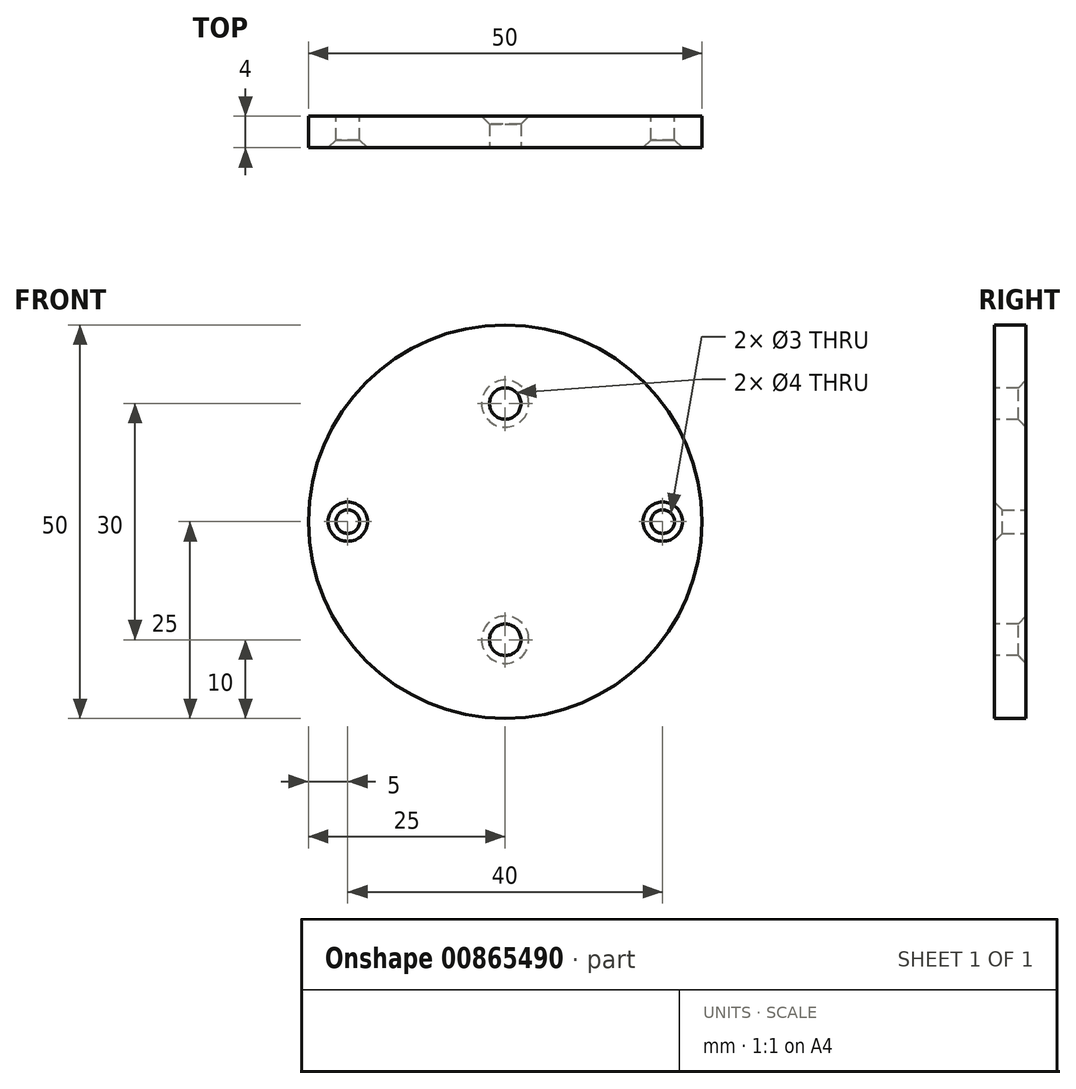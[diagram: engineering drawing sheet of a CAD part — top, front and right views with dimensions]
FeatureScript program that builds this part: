
annotation { "Feature Type Name" : "Feature", "Feature Type Description" : "" }
export const myFeature = defineFeature(function(context is Context, id is Id, definition is map)
    precondition{}
    {
        {
            var Q0;
            Q0=qCreatedBy(makeId("Front.planeOp"),FACE);
            var sketch = newSketch(context, id + "F0", { "sketchPlane" : qUnion([Q0])});
            skCircle(sketch, "E0", {"center": v(0, 0) * mm, "radius": 25 * mm});
            skCircle(sketch, "E1", {"center": v(20, 0) * mm, "radius": 1.5 * mm});
            skCircle(sketch, "E2", {"center": v(-20, 0) * mm, "radius": 1.5 * mm});
            skSolve(sketch);
        }
        {
            var Q0;
            Q0=makeQuery(id+"F0.imprint","IMPRINT",FACE,{"disambiguationData":[TD([[makeQuery(id+"F0.imprint","IMPRINT",EDGE,{"derivedFrom":sQuery(id+"F0.wireOp",EDGE,"E0")}),1.0]])]});
            extrude(context, id + "F1", {"entities" : qUnion([Q0]), "depth" : 4 * mm, "offsetDistance" : 25 * mm});
        }
        {
            var Q0;
            Q0=makeQuery(id+"F1.opExtrude","CAP_EDGE",EDGE,{"disambiguationData":[OSD([sQuery(id+"F0.wireOp",EDGE,"E2")])],"isStart":false});
            var Q1;
            Q1=makeQuery(id+"F1.opExtrude","CAP_EDGE",EDGE,{"disambiguationData":[OSD([sQuery(id+"F0.wireOp",EDGE,"E1")])],"isStart":false});
            chamfer(context, id + "F2", {"entities" : qUnion([Q0, Q1]), "width" : 1 * mm, "tangentPropagation" : true});
        }
        {
            var Q0;
            Q0=makeQuery(id+"F1.opExtrude","CAP_FACE",FACE,{"disambiguationData":[OSD([sQuery(id+"F0.wireOp",EDGE,"E0"),sQuery(id+"F0.wireOp",EDGE,"E1"),sQuery(id+"F0.wireOp",EDGE,"E2")])],"isStart":false});
            var sketch = newSketch(context, id + "F3", { "sketchPlane" : qUnion([Q0])});
            skCircle(sketch, "E3", {"center": v(0, 15) * mm, "radius": 2 * mm});
            skCircle(sketch, "E4", {"center": v(0, -15) * mm, "radius": 2 * mm});
            skSolve(sketch);
        }
        {
            var Q0;
            Q0 = qSketchRegion(id + "F3", true);
            extrude(context, id + "F4", {"entities" : qUnion([Q0]), "operationType" : NewBodyOperationType.REMOVE, "endBound" : BoundingType.THROUGH_ALL, "oppositeDirection" : true, "depth" : 25 * mm, "offsetDistance" : 25 * mm});
        }
        {
            var Q0;
            Q0=makeQuery(id+"F4.boolean.opBoolean","INTERSECT",EDGE,{"derivedFrom":[makeQuery(id+"F1.opExtrude","CAP_FACE",FACE,{"disambiguationData":[OSD([sQuery(id+"F0.wireOp",EDGE,"E0"),sQuery(id+"F0.wireOp",EDGE,"E1"),sQuery(id+"F0.wireOp",EDGE,"E2")])],"isStart":true}),makeQuery(id+"F4.opExtrude","SWEPT_FACE",FACE,{"disambiguationData":[OSD([sQuery(id+"F3.wireOp",EDGE,"E3")])]})]});
            var Q1;
            Q1=makeQuery(id+"F4.boolean.opBoolean","INTERSECT",EDGE,{"derivedFrom":[makeQuery(id+"F1.opExtrude","CAP_FACE",FACE,{"disambiguationData":[OSD([sQuery(id+"F0.wireOp",EDGE,"E0"),sQuery(id+"F0.wireOp",EDGE,"E1"),sQuery(id+"F0.wireOp",EDGE,"E2")])],"isStart":true}),makeQuery(id+"F4.opExtrude","SWEPT_FACE",FACE,{"disambiguationData":[OSD([sQuery(id+"F3.wireOp",EDGE,"E4")])]})]});
            chamfer(context, id + "F5", {"entities" : qUnion([Q0, Q1]), "width" : 1 * mm, "tangentPropagation" : true});
        }
    });
